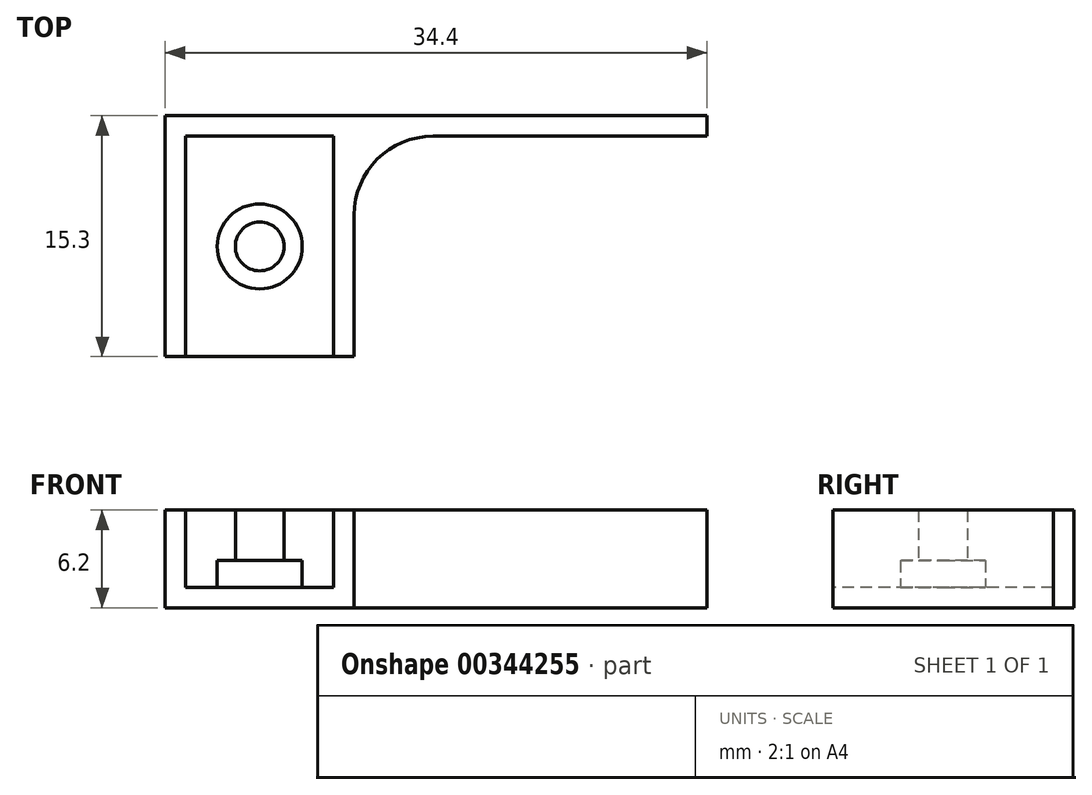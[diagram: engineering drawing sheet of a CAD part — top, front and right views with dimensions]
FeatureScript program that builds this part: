
annotation { "Feature Type Name" : "Feature", "Feature Type Description" : "" }
export const myFeature = defineFeature(function(context is Context, id is Id, definition is map)
    precondition{}
    {
        {
            var Q0;
            Q0=qCreatedBy(makeId("Top.planeOp"),FACE);
            var sketch = newSketch(context, id + "F0", { "sketchPlane" : qUnion([Q0])});
            skLineSegment(sketch, "E0.bottom", {"start": v(0, 0) * mm, "end": v(9.4, 0) * mm});
            skLineSegment(sketch, "E0.top", {"start": v(0, -14) * mm, "end": v(9.4, -14) * mm});
            skLineSegment(sketch, "E0.left", {"start": v(0, 0) * mm, "end": v(0, -14) * mm});
            skLineSegment(sketch, "E0.right", {"start": v(9.4, 0) * mm, "end": v(9.4, -14) * mm});
            skLineSegment(sketch, "E1.top", {"start": v(0, -7) * mm, "end": v(4.7, -7) * mm});
            skLineSegment(sketch, "E1.left", {"start": v(0, 0) * mm, "end": v(0, -7) * mm});
            skLineSegment(sketch, "E1.right", {"start": v(4.7, 0) * mm, "end": v(4.7, -7) * mm});
            skCircle(sketch, "E2", {"center": v(4.7, -7) * mm, "radius": 2.7 * mm});
            skLineSegment(sketch, "E3.bottom", {"start": v(0, 0) * mm, "end": v(-1.3, 0) * mm});
            skLineSegment(sketch, "E3.top", {"start": v(0, -14) * mm, "end": v(-1.3, -14) * mm});
            skLineSegment(sketch, "E3.right", {"start": v(-1.3, 0) * mm, "end": v(-1.3, -14) * mm});
            skLineSegment(sketch, "E4.bottom", {"start": v(9.4, 0) * mm, "end": v(10.7, 0) * mm});
            skLineSegment(sketch, "E4.top", {"start": v(9.4, -14) * mm, "end": v(10.7, -14) * mm});
            skLineSegment(sketch, "E4.right", {"start": v(10.7, 0) * mm, "end": v(10.7, -14) * mm});
            skCircle(sketch, "E5", {"center": v(4.7, -7) * mm, "radius": 1.55 * mm});
            skLineSegment(sketch, "E6.bottom", {"start": v(-1.3, 0) * mm, "end": v(33.1, 0) * mm});
            skLineSegment(sketch, "E6.top", {"start": v(-1.3, 1.3) * mm, "end": v(33.1, 1.3) * mm});
            skLineSegment(sketch, "E6.left", {"start": v(-1.3, 0) * mm, "end": v(-1.3, 1.3) * mm});
            skLineSegment(sketch, "E6.right", {"start": v(33.1, 0) * mm, "end": v(33.1, 1.3) * mm});
            skSolve(sketch);
        }
        {
            var Q0;
            {var subQ0=sQuery(id+"F0.wireOp",EDGE,"E1.right");var subQ1=sQuery(id+"F0.wireOp",EDGE,"E1.top");var subQ2=makeQuery(id+"F0.imprint","INTERSECT",VERTEX,{"derivedFrom":[subQ1,subQ0]});Q0=makeQuery(id+"F0.imprint","IMPRINT",FACE,{"disambiguationData":[TD([[makeQuery(id+"F0.imprint","IMPRINT",EDGE,{"disambiguationData":[TD([[subQ2,1.0]])],"derivedFrom":subQ1}),-1.0]])]});}
            var Q1;
            {var subQ0=sQuery(id+"F0.wireOp",EDGE,"E1.right");var subQ1=sQuery(id+"F0.wireOp",EDGE,"E1.top");var subQ2=makeQuery(id+"F0.imprint","INTERSECT",VERTEX,{"derivedFrom":[subQ1,subQ0]});Q1=makeQuery(id+"F0.imprint","IMPRINT",FACE,{"disambiguationData":[TD([[makeQuery(id+"F0.imprint","IMPRINT",EDGE,{"disambiguationData":[TD([[subQ2,1.0]])],"derivedFrom":subQ1}),1.0]])]});}
            var Q2;
            {var subQ2=sQuery(id+"F0.wireOp",EDGE,"E3.top");Q2=makeQuery(id+"F0.imprint","IMPRINT",FACE,{"disambiguationData":[TD([[makeQuery(id+"F0.imprint","IMPRINT",EDGE,{"derivedFrom":subQ2}),-1.0]])]});}
            var Q3;
            Q3=makeQuery(id+"F0.imprint","IMPRINT",FACE,{"disambiguationData":[TD([[makeQuery(id+"F0.imprint","IMPRINT",EDGE,{"derivedFrom":sQuery(id+"F0.wireOp",EDGE,"E4.top")}),1.0]])]});
            var Q4;
            Q4=makeQuery(id+"F0.imprint","IMPRINT",FACE,{"disambiguationData":[TD([[makeQuery(id+"F0.imprint","IMPRINT",EDGE,{"derivedFrom":sQuery(id+"F0.wireOp",EDGE,"E6.top")}),-1.0]])]});
            extrude(context, id + "F1", {"entities" : qUnion([Q0, Q1, Q2, Q3, Q4]), "depth" : 6.2 * mm});
        }
        {
            var Q0;
            {var subQ0=sQuery(id+"F0.wireOp",EDGE,"E2");var subQ1=sQuery(id+"F0.wireOp",EDGE,"E1.top");var subQ2=makeQuery(id+"F0.imprint","INTERSECT",VERTEX,{"derivedFrom":[subQ1,subQ0]});Q0=makeQuery(id+"F0.imprint","IMPRINT",FACE,{"disambiguationData":[TD([[makeQuery(id+"F0.imprint","IMPRINT",EDGE,{"disambiguationData":[TD([[subQ2,-1.0]])],"derivedFrom":subQ1}),-1.0]])]});}
            var Q1;
            {var subQ0=sQuery(id+"F0.wireOp",EDGE,"E2");var subQ1=sQuery(id+"F0.wireOp",EDGE,"E1.top");var subQ2=makeQuery(id+"F0.imprint","INTERSECT",VERTEX,{"derivedFrom":[subQ1,subQ0]});Q1=makeQuery(id+"F0.imprint","IMPRINT",FACE,{"disambiguationData":[TD([[makeQuery(id+"F0.imprint","IMPRINT",EDGE,{"disambiguationData":[TD([[subQ2,-1.0]])],"derivedFrom":subQ1}),1.0]])]});}
            extrude(context, id + "F2", {"entities" : qUnion([Q0, Q1]), "operationType" : NewBodyOperationType.ADD, "depth" : 3 * mm});
        }
        {
            var Q0;
            {var subQ5=sQuery(id+"F0.wireOp",EDGE,"E0.top");Q0=makeQuery(id+"F0.imprint","IMPRINT",FACE,{"disambiguationData":[TD([[makeQuery(id+"F0.imprint","IMPRINT",EDGE,{"derivedFrom":subQ5}),1.0]])]});}
            var Q1;
            {var subQ1=sQuery(id+"F0.wireOp",EDGE,"E1.top");var subQ7=sQuery(id+"F0.wireOp",EDGE,"E0.left");var subQ8=makeQuery(id+"F0.imprint","INTERSECT",VERTEX,{"derivedFrom":[subQ1,subQ7]});Q1=makeQuery(id+"F0.imprint","IMPRINT",FACE,{"disambiguationData":[TD([[makeQuery(id+"F0.imprint","IMPRINT",EDGE,{"disambiguationData":[TD([[subQ8,-1.0]])],"derivedFrom":subQ1}),1.0]])]});}
            extrude(context, id + "F3", {"entities" : qUnion([Q0, Q1]), "operationType" : NewBodyOperationType.ADD, "depth" : 1.3 * mm});
        }
        {
            var Q0;
            Q0=makeQuery(id+"F1.opExtrude","SWEPT_EDGE",EDGE,{"disambiguationData":[OSD([sQuery(id+"F0.wireOp",EDGE,"E4.right"),sQuery(id+"F0.wireOp",EDGE,"E6.bottom")])]});
            fillet(context, id + "F4", {"entities" : qUnion([Q0]), "radius" : 5 * mm, "tangentPropagation" : true, "allowEdgeOverflow" : false});
        }
    });
